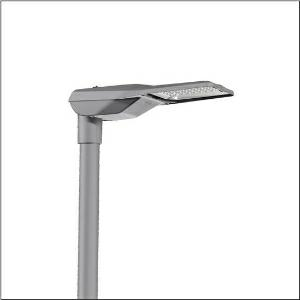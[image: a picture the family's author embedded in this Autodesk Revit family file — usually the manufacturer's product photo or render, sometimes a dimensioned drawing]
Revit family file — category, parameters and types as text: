
# Revit family: streetlight_sl_21_mini___stw1_0a_5xe2e33s08gb_da95
name_source: partatom
category: Lighting Fixtures
units: mm (PartAtom-declared; Revit-internal decimal feet)

## family parameters
Cut with Voids When Loaded = No
Host = Face
Light Source = No
Part Type = Normal
Room Calculation Point = No
Round Connector Dimension = Use Diameter
Shared = No

## types (1)
- --- (1 x LED, 5940 lm, 40.4 W, 3000K)
    Apparent Load = 40 VA
    CIE Flux Codes = 38 75 98 100 100
    Color Rendering = 70
    Color Temperature = 3000K
    Default Elevation = 1800 mm
    Description = Streetlight SL 21 mini, mast luminaire, primary light control with lens, of PMMA, primary optical cover: cover, of toughened safety glass, transparent, light distribution: STW1.0a, light emission: direct distribution, primary light characteristic: asymmetric, installation type: side-entry, post-top, LED, High Power LED, rated luminous flux: 5.940lm, luminous efficacy: 147lm/W, light colour: 730, colour temperature: 3000K, control gear: D4i, control: overheat protection, constant luminous flux control, time-dependent luminous flux control, flexible luminous flux parameterisation, pre-setting: logarithmic dimming characteristic, mains connection: 220..240V, AC, 50/60Hz, start of lifetime: 40W, end of service life: 41W, reduction: 19W, luminaire housing, of diecast aluminium, powder-coated, Siteco® metallic grey (DB 702S), corrosivity category C5 mid according to DIN EN ISO 12944, please order mast flange separately, inclination adjustable: 0°, 5°, 10°, 15°, sealing non-destructively replaceable, multi-level sealing system, length: 628mm, width: 235mm, height: 110mm, mast flange for spigot size: 42mm (side-entry): 5XC10008XM4, 60/48mm (side-entry/post-top): 5XC10108XM2, 76/60mm (side-entry/post-top): 5XC10108XM1, mounting height: 4..8m, Smart Interface above, protection rating (complete): IP66, insulation class (complete): insulation class II (safety insulation), certification: CE, ENEC, ENEC+, VDE, impact resistance: IK10, permissible operating ambient temperature for outdoor applications: -40..+50°C, standard-compliant lighting for roads and squares, packaging unit: 1 piece

Light Distribution: STW1.0a
    Height = 110 mm
    Lamp = 1 x LED
    Lamp Light Flux = 5940 lm
    Lamp Power = 40.4 W
    Lamp count = 1
    Length = 625 mm
    Luminous efficacy = 147 lm/W
    Manufacturer = Siteco
    ModVariant = No
    Model = 5XE2E33S08GB
    Number of Poles = 1
    OnlyDefault = Yes
    Power Factor = 1
    Product Name = Streetlight SL 21 mini | STW1.0a
    Product group = mast luminaire | pylon top
    ProductGroupID = 6100
    Protection Class = Protection class II
    Protection Degree = IP 66
    RLX_Detail_Level = 1
    RLX_Emergency_Light_Flux = 0 lm
    RLX_Emergency_Type = 0
    RLX_Emergency_Type_DB = No
    RlxData = <blob elided: 26217 chars, md5=3c9f8cc6>
    Socket = socket
    Standby Power = 0 W
    System Light Flux = 5940 lm
    System Power = 40 W
    Type Comments = factory setting: luminous flux: 100 % | dim-lin: 254 | 812 mA
    Type Image = l_1003515.jpg
    URL = http://relux.com
    VarID = @adj_208745
    Voltage = 0 V
    Weight = 0.00 kg
    Width = 234 mm

## geometry (parser evidence)
native form markers: Blend x4, Sweep x10
no freeform markers — native parametric forms only
